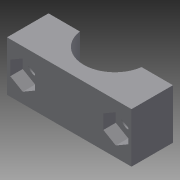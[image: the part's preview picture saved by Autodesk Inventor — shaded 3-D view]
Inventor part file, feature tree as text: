
AUTODESK INVENTOR PART (.ipt)
format: ipt  version: 2013 SP2 (Build 170200200, 200)  size: 109,056 bytes
history: native  units: mm
features: extrude x3, sketch x3
ambient origin geometry x8: Origin, YZ Plane, XZ Plane, XY Plane, X Axis, Y Axis, Z Axis, Center Point
bodies: Solid1 (feature_tree)
feature tree (6):
  extrude  "Extrusion1"  Depth=10.0mm
  extrude  "Extrusion2"  Depth=1.0mm
  extrude  "Extrusion3"  Depth=3.3mm
  sketch  "Sketch1"  dims[d0=30.0mm d1=10.0mm]
  sketch  "Sketch2"  dims[d2=15.0mm d3=1.0mm]
  sketch  "Sketch3"  dims[d4=12.0mm d5=0.0mm d6=3.3mm d7=3.3mm d8=15.0mm d9=0.0mm d10=6.0mm d11=6.0mm d12=3.0mm d13=0.0mm]
